# Revit family: RN 91026 Optifitt-Serra-Réduction
name_source: partatom
category: Rohrformteile
units: mm (PartAtom-declared; Revit-internal decimal feet)

## family parameters
Arbeitsebenenbasiert = Nein
Beim Laden mit Abzugskörper schneiden = Nein
Bemaßung runder Anschluss = Durchmesser verwenden
Gemeinsam genutzt = Nein
Immer vertikal = Ja
Teiletyp = Übergang

## types (7) — shared parameters
1.010.00.2 Blattnummer der Richtlinie = 29
1.010.00.3 Ausgabedatum (Monat) der Richtlinie = 201308
1.010.00.4 Herstellername = R. Nussbaum AG
1.010.00.5 Revisionsdatum der Datei = 20190521
1.010.00.6 Webadresse des Herstellers = http://www.nussbaum.ch
1.100.00.4 Produktbezeichnung = Versorgung
1.110.00.2 Index = 3
1.110.00.4 Produktbezeichnung = Optifitt-Serra
1.960/3L.00.8 Link (URL) = https://www.nussbaum.ch
29.700.00.4 Produktname = Optifitt-Serra-Reduktion
29.700.00.5 Produktkennung = 2
29.700.00.6 Querschnittsform = 1
29.700.00.7 Nennweitensystem = DN
29.700.00.8 Nenndrucksystem = PN
29.710.02.4 Nenndruck = 16
29.710.02.5 max. zul. Überdruck [hPa] = 1600
29.710.02.7 max. zul. Dauer-Betriebsdruck [hPa] = 1600
29.710.02.9 max. zul. Dauer-Betriebstemperatur [°C] = 90
Connector Visibility = Nein
EnclosingSpace Visibility = Nein
Hersteller = R. Nussbaum AG
URL = https://www.nussbaum.ch

## per-type parameters (varying)
| type | 1.800.00.3 TGA-Nummer | 1.800.00.4 Kommentarfeld | 1.810.00.3 Hersteller-Bestellnummer | 1.810.00.4 DATANORM-Nummer | 1.810.00.5 StLB-Nummer | 1.810.00.6 GTIN-Nummer | 29.710.02.10 Formstück-Gewicht [kg] | 29.710.02.3 Benennung | CONNECTOR0_DIAMETER_dX_0r | CONNECTOR0_dX_01 | CONNECTOR0_ref_dX | CONNECTOR1_DIAMETER_dX_0r | CONNECTOR1_dX_00 | CONNECTOR1_dX_01 | CONNECTOR1_ref_dX | Modell | R. Nussbaum AG 91026.71 de Visibility | R. Nussbaum AG 91026.72 de Visibility | R. Nussbaum AG 91026.73 de Visibility | R. Nussbaum AG 91026.74 de Visibility | R. Nussbaum AG 91026.75 de Visibility | R. Nussbaum AG 91026.76 de Visibility | R. Nussbaum AG 91026.78 de Visibility | Typenkommentare |
| DN=32x25 | 01900300000000000000000000000000000000000000000014000000000000000042 | 91026.78, Optifitt-Serra-Reduktion, DN=32x25, L=31, R=1¼, Rp=1 | 91026.78 | 91026.78 | 214.535 | 7612945036018 | 0.159 | Optifitt-Serra-Reduktion, DN=32x25, L=31, R=1¼, Rp=1 | 25 mm | 17 mm | 17 mm | 32 mm | 12 mm  [stored 0.0393701 ft] | 31 mm  [stored 0.101706 ft] | 31 mm  [stored 0.101706 ft] | 91026.78 | Nein | Nein | Nein | Nein | Nein | Nein | Ja | Optifitt-Serra-Réduction  DN=32x25 |
| DN=25x20 | 01900300000000000000000000000000000000000000000014000000000000000041 | 91026.76, Optifitt-Serra-Reduktion, DN=25x20, L=28, R=1, Rp=¾ | 91026.76 | 91026.76 | 214.534 | 7612945035998 | 0.077 | Optifitt-Serra-Reduktion, DN=25x20, L=28, R=1, Rp=¾ | 20 mm | 15 mm | 15 mm | 25 mm | 11 mm | 28 mm | 28 mm | 91026.76 | Nein | Nein | Nein | Nein | Nein | Ja | Nein | Optifitt-Serra-Réduction  DN=25x20 |
| DN=25x15 | 01900300000000000000000000000000000000000000000014000000000000000040 | 91026.75, Optifitt-Serra-Reduktion, DN=25x15, L=28, R=1, Rp=½ | 91026.75 | 91026.75 |  | 7612945035981 | 0.102 | Optifitt-Serra-Reduktion, DN=25x15, L=28, R=1, Rp=½ | 15 mm | 13 mm  [stored 0.0426509 ft] | 13 mm  [stored 0.0426509 ft] | 25 mm | 11 mm | 28 mm | 28 mm | 91026.75 | Nein | Nein | Nein | Nein | Ja | Nein | Nein | Optifitt-Serra-Réduction  DN=25x15 |
| DN=20x15 | 01900300000000000000000000000000000000000000000014000000000000000039 | 91026.74, Optifitt-Serra-Reduktion, DN=20x15, L=24, R=¾, Rp=½ | 91026.74 | 91026.74 | 214.533 | 7612945035974 | 0.042 | Optifitt-Serra-Reduktion, DN=20x15, L=24, R=¾, Rp=½ | 15 mm | 13 mm  [stored 0.0426509 ft] | 13 mm  [stored 0.0426509 ft] | 20 mm | 8 mm  [stored 0.0262467 ft] | 23 mm  [stored 0.0754593 ft] | 23 mm  [stored 0.0754593 ft] | 91026.74 | Nein | Nein | Nein | Ja | Nein | Nein | Nein | Optifitt-Serra-Réduction  DN=20x15 |
| DN=20x12 | 01900300000000000000000000000000000000000000000014000000000000000038 | 91026.73, Optifitt-Serra-Reduktion, DN=20x12, L=23, R=¾, Rp=3/8 | 91026.73 | 91026.73 |  | 7612945035967 | 0.052 | Optifitt-Serra-Reduktion, DN=20x12, L=23, R=¾, Rp=3/8 | 10 mm  [stored 0.0328084 ft] | 10 mm  [stored 0.0328084 ft] | 10 mm  [stored 0.0328084 ft] | 20 mm | 8 mm  [stored 0.0262467 ft] | 23 mm  [stored 0.0754593 ft] | 23 mm  [stored 0.0754593 ft] | 91026.73 | Nein | Nein | Ja | Nein | Nein | Nein | Nein | Optifitt-Serra-Réduction  DN=20x12 |
| DN=15x12 | 01900300000000000000000000000000000000000000000014000000000000000037 | 91026.72, Optifitt-Serra-Reduktion, DN=15x12, L=22, R=½, Rp=3/8 | 91026.72 | 91026.72 | 214.532 | 7612945035950 | 0.024 | Optifitt-Serra-Reduktion, DN=15x12, L=22, R=½, Rp=3/8 | 10 mm  [stored 0.0328084 ft] | 10 mm  [stored 0.0328084 ft] | 10 mm  [stored 0.0328084 ft] | 15 mm | 9 mm | 22 mm | 22 mm | 91026.72 | Nein | Ja | Nein | Nein | Nein | Nein | Nein | Optifitt-Serra-Réduction  DN=15x12 |
| DN=12x10 | 01900300000000000000000000000000000000000000000014000000000000000036 | 91026.71, Optifitt-Serra-Reduktion, DN=12x10, L=17, R=3/8, Rp=¼ | 91026.71 | 91026.71 | 214.531 | 7612945035943 | 0.014 | Optifitt-Serra-Reduktion, DN=12x10, L=17, R=3/8, Rp=¼ | 10 mm  [stored 0.0328084 ft] | 8 mm  [stored 0.0262467 ft] | 8 mm  [stored 0.0262467 ft] | 10 mm  [stored 0.0328084 ft] | 7 mm  [stored 0.0229659 ft] | 17 mm | 17 mm | 91026.71 | Ja | Nein | Nein | Nein | Nein | Nein | Nein | Optifitt-Serra-Réduction  DN=12x10 |

note: [stored X ft] marks values corroborated as IEEE doubles in the binary element streams (Revit-internal decimal feet)

## geometry (parser evidence)
native form markers: Sweep x1
no freeform markers — native parametric forms only
